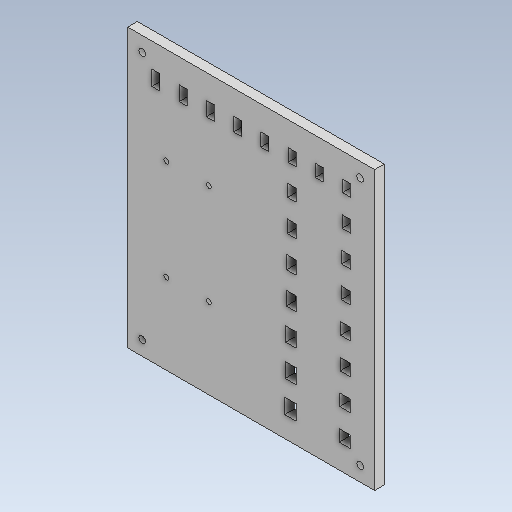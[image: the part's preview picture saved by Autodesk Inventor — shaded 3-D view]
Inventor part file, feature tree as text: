
AUTODESK INVENTOR PART (.ipt)
format: ipt  version: 2025.2 (Build 292293000, 293)  size: 562,688 bytes
history: native  units: mm
features: sketch x4, extrude x3, hole x1
ambient origin geometry x8: Origin, YZ Plane, XZ Plane, XY Plane, X Axis, Y Axis, Z Axis, Center Point
bodies: Volumenkörper1 (feature_tree)
feature tree (8):
  extrude  "Extrusion1"  Depth=255.6mm
  extrude  "Extrusion4"  Depth=10.0mm TaperAngle=0.0deg
  extrude  "Extrusion5"  Depth=12.2mm
  hole  "Bohrung1"  [1 undecoded]
  sketch  "Skizze1"  dims[d0=287.6mm d1=255.6mm]
  sketch  "Skizze4"  dims[d2=10.0mm d3=0.0mm d8=30.0mm d9=0.0mm]
  sketch  "Skizze5"  dims[d10=8.2mm d11=12.2mm]
  sketch  "Skizze6"  dims[d17=12.2mm d18=9.2mm d19=12.2mm d20=9.7mm d21=12.2mm d22=10.2mm d23=12.2mm d24=10.7mm d25=12.2mm d27=12.2mm d29=13.7mm d30=14.2mm d32=14.7mm d53=11.2mm d60=12.2mm d61=11.7mm d64=12.7mm d65=8.2mm d79=12.7mm d80=13.2mm d81=9.2mm d82=13.7mm d83=9.7mm d84=14.2mm d85=10.2mm d86=14.7mm d87=10.7mm d88=15.2mm d89=11.2mm d90=15.7mm d91=11.7mm d110=5.0mm d114=30.0mm d115=0.0mm d116=5.0mm d119=100.0mm d149=15.7mm d152=8.2mm d153=8.2mm d155=20.0mm d156=8.2mm d159=20.0mm d160=20.0mm d162=20.0mm d163=20.0mm d164=20.0mm d165=20.0mm d166=20.0mm d167=20.0mm d168=20.0mm d169=20.0mm d179=0.0mm d180=0.0mm d181=0.0mm d182=0.0mm d183=0.0mm d184=0.0mm d187=19.0mm d188=18.5mm d189=18.0mm d191=17.5mm d192=0.0mm d197=8.2mm d198=15.2mm d199=20.0mm d200=8.2mm d201=20.0mm d203=8.2mm d205=13.2mm d206=0.0mm d207=8.7mm d209=45.8mm d219=8.7mm d224=5.0mm d225=5.0mm d230=104.0mm d231=44.0mm d233=40.0mm d234=0.0mm d239=0.0mm d240=0.0mm d241=17.0mm d245=0.0mm d247=0.0mm d248=0.0mm d249=0.0mm d250=0.0mm d251=19.5mm d254=19.0mm d258=7.0mm d259=6.0mm d260=4.0mm d261=2.0mm d262=90.0deg d263=10.0mm d264=0.0mm d265=15.0mm d266=15.0mm d267=15.0mm d268=15.0mm d269=15.0mm d270=15.0mm d271=15.0mm d272=15.0mm d275=25.0mm d276=25.0mm d278=20.0mm d280=25.0mm d281=25.0mm d283=25.0mm d284=25.0mm]
note: 1 required parameter value undecoded (feature->parameter linkage not recoverable at this tier; creation-order binding heuristic only, values carry confidence <= 0.55)
